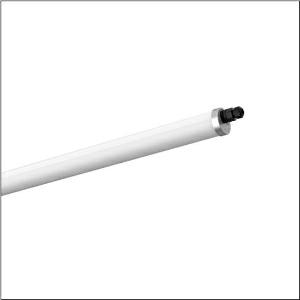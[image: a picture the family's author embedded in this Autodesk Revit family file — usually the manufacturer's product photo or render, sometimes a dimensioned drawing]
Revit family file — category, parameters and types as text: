
# Revit family: monsun_r__31_tube_51ft107n460a_2b58
name_source: partatom
category: Lighting Fixtures
units: mm (PartAtom-declared; Revit-internal decimal feet)

## family parameters
Cut with Voids When Loaded = No
Host = Face
Light Source = No
Part Type = Normal
Room Calculation Point = No
Round Connector Dimension = Use Diameter
Shared = No

## types (1)
- Monsun® 31 Tube (1 x LED, 6500 lm, 40 W, 4000K)
    Apparent Load = 40 VA
    CIE Flux Codes = 42 71 90 91 100
    Color Rendering = 80
    Color Temperature = 4000K
    Default Elevation = 1800 mm
    Description = Monsun® 31 Tube, tubular luminaire, primary optical cover: diffuser, of PMMA, light emission: direct distribution, primary light characteristic: symmetric, installation type: suspended mounting, surface-mounted, LED, rated luminous flux: 6.500lm, luminous efficacy: 160lm/W, light colour: 840, colour temperature: 4000K, with with 1 terminal, 3-pole, max. 2.5mm², through-wiring: 3x 1.5mm², mains connection: 220..240V, AC, 50/60Hz, rated input power: 40W, housing, cylindrical, of PMMA, semi-transparent, matt white, with luminaire and ceiling fastening, V4A, mounting with brackets of stainless steel, length: 1.560mm, diameter: 75mm, end cap, of stainless steel (V4A), protection rating (complete): IP67/IP69K, insulation class (complete): insulation class I (protective earthing), certification: CE, UKCA, impact resistance: IK07, permissible operating ambient temperature: -20..+40°C, corresponds to IFS (International Featured Standards) requirements for safety and quality in the food industry, usage in unprotected outdoor area possible with horizontal mounting, contact your sales advisor before using the luminaires in applications with unclear chemical exposure, large temperature fluctuations or condensation-forming humidity, packaging unit: 1 piece
    Height = 83 mm
    Lamp = 1 x LED
    Lamp Light Flux = 6500 lm
    Lamp Power = 40 W
    Lamp count = 1
    Length = 1560 mm
    Luminous efficacy = 163 lm/W
    Manufacturer = Siteco
    ModVariant = No
    Model = 51FT107N460A
    Mounting Place = Ceiling
    Mounting Type = Pendant
    Number of Poles = 1
    OnlyDefault = Yes
    Power Factor = 1
    Product Name = Monsun® 31 Tube
    Product group = tubular luminaire
    ProductGroupID = 906
    Protection Class = Protection class I
    RLX_Detail_Level = 1
    RLX_Emergency_Light_Flux = 0 lm
    RLX_Emergency_Type = 0
    RLX_Emergency_Type_DB = No
    RlxData = <blob elided: 25273 chars, md5=789960f2>
    Socket = socket
    Standby Power = 0 W
    System Light Flux = 6500 lm
    System Power = 40 W
    Type Comments = Product without accessories
    Type Image = l_1228461.jpg
    URL = http://relux.com
    VarID = ---
    Voltage = 0 V
    Weight = 0.00 kg
    Width = 75 mm

## geometry (parser evidence)
native form markers: Blend x4, Sweep x11
no freeform markers — native parametric forms only
